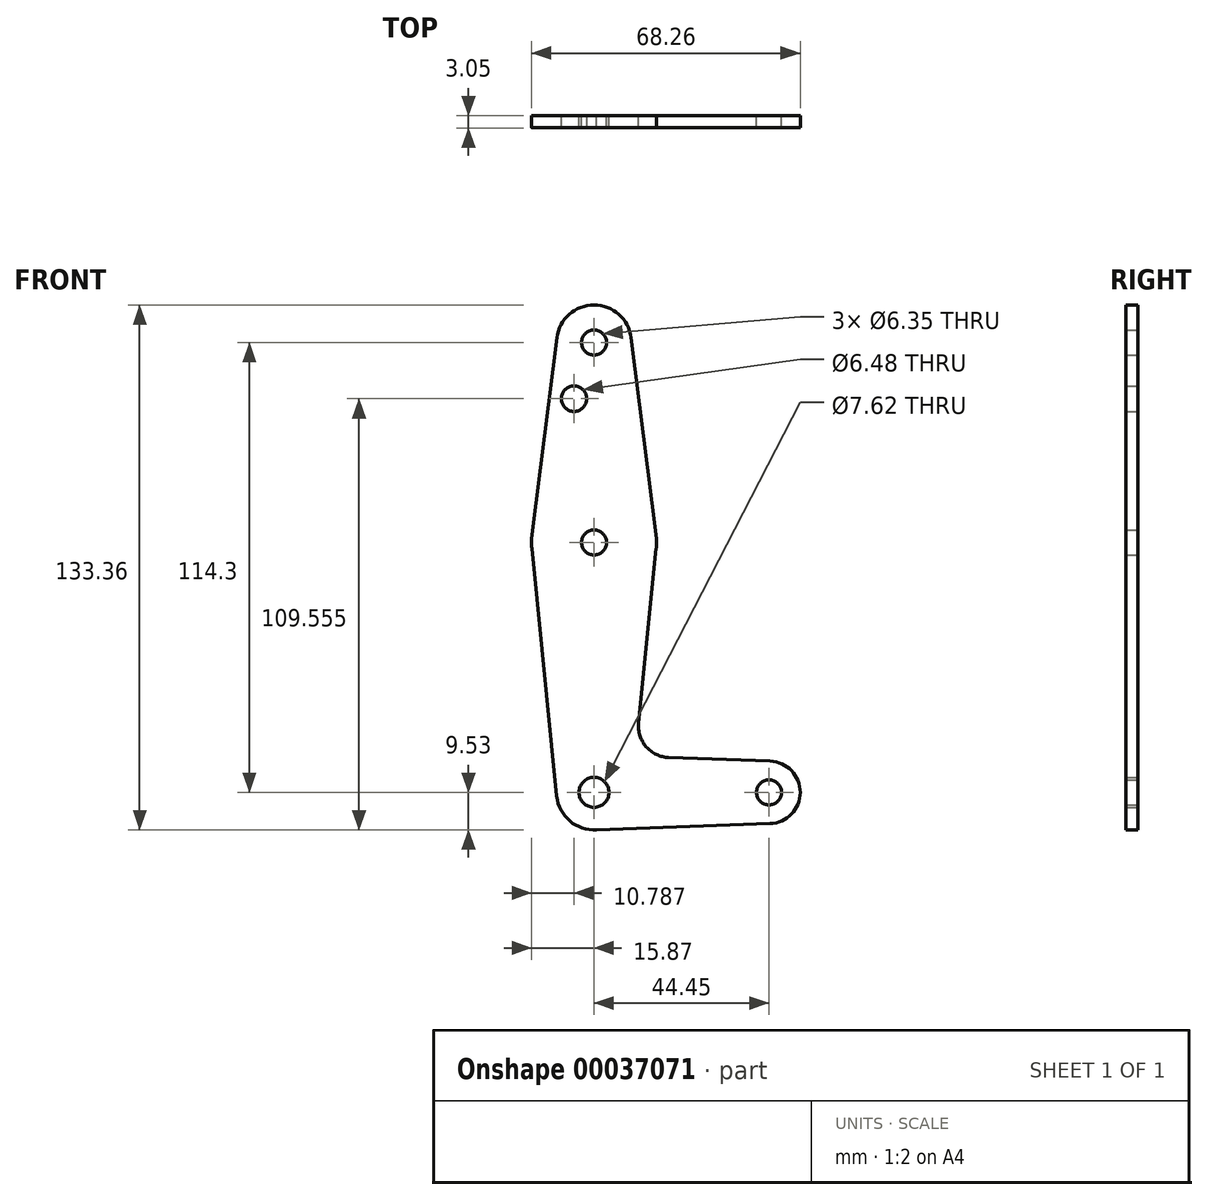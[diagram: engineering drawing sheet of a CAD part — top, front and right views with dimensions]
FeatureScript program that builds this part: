
annotation { "Feature Type Name" : "Feature", "Feature Type Description" : "" }
export const myFeature = defineFeature(function(context is Context, id is Id, definition is map)
    precondition{}
    {
        {
            var Q0;
            Q0=qCreatedBy(makeId("Front.planeOp"),FACE);
            var sketch = newSketch(context, id + "F0", { "sketchPlane" : qUnion([Q0])});
            skLineSegment(sketch, "E0", {"start": v(0, 0) * mm, "end": v(0, 63.5) * mm, "construction": true});
            skLineSegment(sketch, "E1", {"start": v(0, 63.5) * mm, "end": v(0, 114.3) * mm, "construction": true});
            skLineSegment(sketch, "E2", {"start": v(0, 0) * mm, "end": v(44.45, 0) * mm, "construction": true});
            skCircle(sketch, "E3", {"center": v(0, 114.3) * mm, "radius": 9.53 * mm});
            skCircle(sketch, "E4", {"center": v(0, 63.5) * mm, "radius": 15.88 * mm});
            skCircle(sketch, "E5", {"center": v(0, 0) * mm, "radius": 9.53 * mm});
            skCircle(sketch, "E6", {"center": v(44.45, 0) * mm, "radius": 7.94 * mm});
            skLineSegment(sketch, "E7", {"start": v(-9.45, 115.5) * mm, "end": v(-15.75, 65.48) * mm});
            skLineSegment(sketch, "E8", {"start": v(9.45, 115.5) * mm, "end": v(15.75, 65.48) * mm});
            skLineSegment(sketch, "E9", {"start": v(15.8, 61.91) * mm, "end": v(11.34, 17.6) * mm});
            skLineSegment(sketch, "E10", {"start": v(-15.8, 61.91) * mm, "end": v(-9.48, -0.95) * mm});
            skLineSegment(sketch, "E11", {"start": v(18.97, 8.85) * mm, "end": v(44.73, 7.93) * mm});
            skLineSegment(sketch, "E12", {"start": v(0, -9.53) * mm, "end": v(44.73, -7.93) * mm});
            skCircle(sketch, "E13", {"center": v(0, 114.3) * mm, "radius": 3.18 * mm});
            skCircle(sketch, "E14", {"center": v(0, 63.5) * mm, "radius": 3.18 * mm});
            skCircle(sketch, "E15", {"center": v(0, 0) * mm, "radius": 3.81 * mm});
            skCircle(sketch, "E16", {"center": v(44.45, 0) * mm, "radius": 3.18 * mm});
            skCircle(sketch, "E17", {"center": v(-5.08, 100.03) * mm, "radius": 3.24 * mm});
            skArc(sketch, "E18.filletArc", {"start": v(11.34, 17.6) * mm, "mid": v(13.26, 11.57) * mm, "end": v(18.97, 8.85) * mm});
            skSolve(sketch);
        }
        {
            var Q0;
            Q0 = qSketchRegion(id + "F0", true);
            extrude(context, id + "F1", {"entities" : qUnion([Q0]), "depth" : 3.05 * mm});
        }
    });
